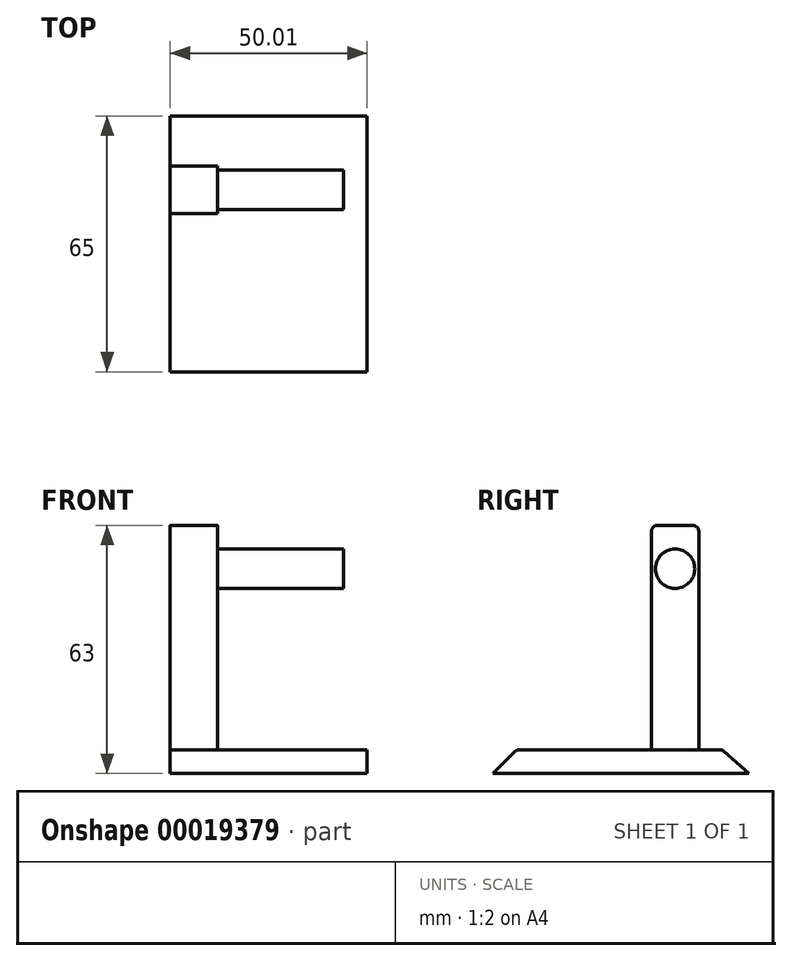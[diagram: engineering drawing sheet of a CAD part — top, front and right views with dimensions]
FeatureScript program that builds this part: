
annotation { "Feature Type Name" : "Feature", "Feature Type Description" : "" }
export const myFeature = defineFeature(function(context is Context, id is Id, definition is map)
    precondition{}
    {
        {
            var Q0;
            Q0=qCreatedBy(makeId("Top.planeOp"),FACE);
            var sketch = newSketch(context, id + "F0", { "sketchPlane" : qUnion([Q0])});
            skLineSegment(sketch, "E0.bottom", {"start": v(-22.2, 50.92) * mm, "end": v(27.8, 50.92) * mm});
            skLineSegment(sketch, "E0.top", {"start": v(-22.2, -14.08) * mm, "end": v(27.8, -14.08) * mm});
            skLineSegment(sketch, "E0.left", {"start": v(-22.2, 50.92) * mm, "end": v(-22.2, -14.08) * mm});
            skLineSegment(sketch, "E0.right", {"start": v(27.8, 50.92) * mm, "end": v(27.8, -14.08) * mm});
            skSolve(sketch);
        }
        {
            var Q0;
            Q0=qCreatedBy(makeId("Top.planeOp"),FACE);
            cPlane(context, id + "F1", {"entities" : qUnion([Q0]), "cplaneType" : CPlaneType.OFFSET, "offset" : 6 * mm, "width" : 150 * mm, "height" : 150 * mm});
        }
        {
            var Q0;
            Q0=qCreatedBy(id+"F1.planeOp",FACE);
            var sketch = newSketch(context, id + "F2", { "sketchPlane" : qUnion([Q0])});
            skLineSegment(sketch, "E1.bottom", {"start": v(-22.2, 44.19) * mm, "end": v(27.8, 44.19) * mm});
            skLineSegment(sketch, "E1.top", {"start": v(-22.2, -8.01) * mm, "end": v(27.8, -8.01) * mm});
            skLineSegment(sketch, "E1.left", {"start": v(-22.2, 44.19) * mm, "end": v(-22.2, -8.01) * mm});
            skLineSegment(sketch, "E1.right", {"start": v(27.8, 44.19) * mm, "end": v(27.8, -8.01) * mm});
            skSolve(sketch);
        }
        {
            var Q0;
            Q0=makeQuery(id+"F0.imprint","IMPRINT",FACE,{"disambiguationData":[TD([[makeQuery(id+"F0.imprint","IMPRINT",EDGE,{"derivedFrom":sQuery(id+"F0.wireOp",EDGE,"E0.bottom")}),-1.0]])]});
            var Q1;
            Q1=makeQuery(id+"F2.imprint","IMPRINT",FACE,{"disambiguationData":[TD([[makeQuery(id+"F2.imprint","IMPRINT",EDGE,{"derivedFrom":sQuery(id+"F2.wireOp",EDGE,"E1.bottom")}),-1.0]])]});
            loft(context, id + "F3", {"sheetProfilesArray" : [{ "sheetProfileEntities" : qUnion([Q0]) }, { "sheetProfileEntities" : qUnion([Q1]) }]});
        }
        {
            var Q0;
            Q0=makeQuery(id+"F3.opLoft","CAP_FACE",FACE,{"disambiguationData":[OSD([makeQuery(id+"F2.imprint","IMPRINT",FACE,{"disambiguationData":[TD([[makeQuery(id+"F2.imprint","IMPRINT",EDGE,{"derivedFrom":sQuery(id+"F2.wireOp",EDGE,"E1.bottom")}),-1.0]])]})])],"isStart":true});
            var sketch = newSketch(context, id + "F4", { "sketchPlane" : qUnion([Q0])});
            skLineSegment(sketch, "E2", {"start": v(-16.77, 44.19) * mm, "end": v(-16.77, 38.19) * mm});
            skLineSegment(sketch, "E3.bottom", {"start": v(-22.2, 38.19) * mm, "end": v(-10.2, 38.19) * mm});
            skLineSegment(sketch, "E3.top", {"start": v(-22.2, 26.19) * mm, "end": v(-10.2, 26.19) * mm});
            skLineSegment(sketch, "E3.left", {"start": v(-22.2, 38.19) * mm, "end": v(-22.2, 26.19) * mm});
            skLineSegment(sketch, "E3.right", {"start": v(-10.2, 38.19) * mm, "end": v(-10.2, 26.19) * mm});
            skSolve(sketch);
        }
        {
            var Q0;
            Q0=makeQuery(id+"F4.imprint","IMPRINT",FACE,{"disambiguationData":[TD([[makeQuery(id+"F4.imprint","IMPRINT",EDGE,{"derivedFrom":sQuery(id+"F4.wireOp",EDGE,"E3.top")}),1.0]])]});
            extrude(context, id + "F5", {"entities" : qUnion([Q0]), "operationType" : NewBodyOperationType.ADD, "depth" : 57 * mm});
        }
        {
            var Q0;
            Q0=makeQuery(id+"F5.opExtrude","SWEPT_FACE",FACE,{"disambiguationData":[OSD([sQuery(id+"F4.wireOp",EDGE,"E3.right")])]});
            var sketch = newSketch(context, id + "F6", { "sketchPlane" : qUnion([Q0])});
            skLineSegment(sketch, "E4", {"start": v(32.19, 63) * mm, "end": v(32.19, 57) * mm});
            skCircle(sketch, "E5", {"center": v(32.17, 52) * mm, "radius": 5 * mm});
            skLineSegment(sketch, "E6", {"start": v(26.19, 51.57) * mm, "end": v(27.19, 51.57) * mm});
            skSolve(sketch);
        }
        {
            var Q0;
            {var subQ0=sQuery(id+"F6.wireOp",EDGE,"E5");var subQ2=makeQuery(id+"F6.imprint","INTERSECT",VERTEX,{"derivedFrom":[sQuery(id+"F6.wireOp",EDGE,"E4"),subQ0]});Q0=makeQuery(id+"F6.imprint","IMPRINT",FACE,{"disambiguationData":[TD([[makeQuery(id+"F6.imprint","IMPRINT",EDGE,{"disambiguationData":[TD([[subQ2,-1.0]])],"derivedFrom":subQ0}),1.0]])]});}
            extrude(context, id + "F7", {"entities" : qUnion([Q0]), "operationType" : NewBodyOperationType.ADD, "depth" : 32 * mm});
        }
        {
            var Q0;
            Q0=makeQuery(id+"F5.opExtrude","CAP_EDGE",EDGE,{"disambiguationData":[OSD([sQuery(id+"F4.wireOp",EDGE,"E3.top")])],"isStart":false});
            var Q1;
            Q1=makeQuery(id+"F5.opExtrude","CAP_EDGE",EDGE,{"disambiguationData":[OSD([sQuery(id+"F4.wireOp",EDGE,"E3.bottom")])],"isStart":false});
            var Q2;
            Q2=makeQuery(id+"F3.opLoft","MID_CAP_EDGE",EDGE,{"disambiguationData":[OSD([sQuery(id+"F2.wireOp",EDGE,"E1.top"),sQuery(id+"F2.wireOp",EDGE,"E1.left"),sQuery(id+"F2.wireOp",EDGE,"E1.right")])],"capPos":1.0});
            var Q3;
            Q3=makeQuery(id+"F3.opLoft","MID_CAP_EDGE",EDGE,{"disambiguationData":[OSD([sQuery(id+"F2.wireOp",EDGE,"E1.bottom"),sQuery(id+"F2.wireOp",EDGE,"E1.left"),sQuery(id+"F2.wireOp",EDGE,"E1.right")])],"capPos":1.0});
            fillet(context, id + "F8", {"entities" : qUnion([Q0, Q1, Q2, Q3]), "radius" : 1.5 * mm, "tangentPropagation" : true, "allowEdgeOverflow" : false});
        }
    });
